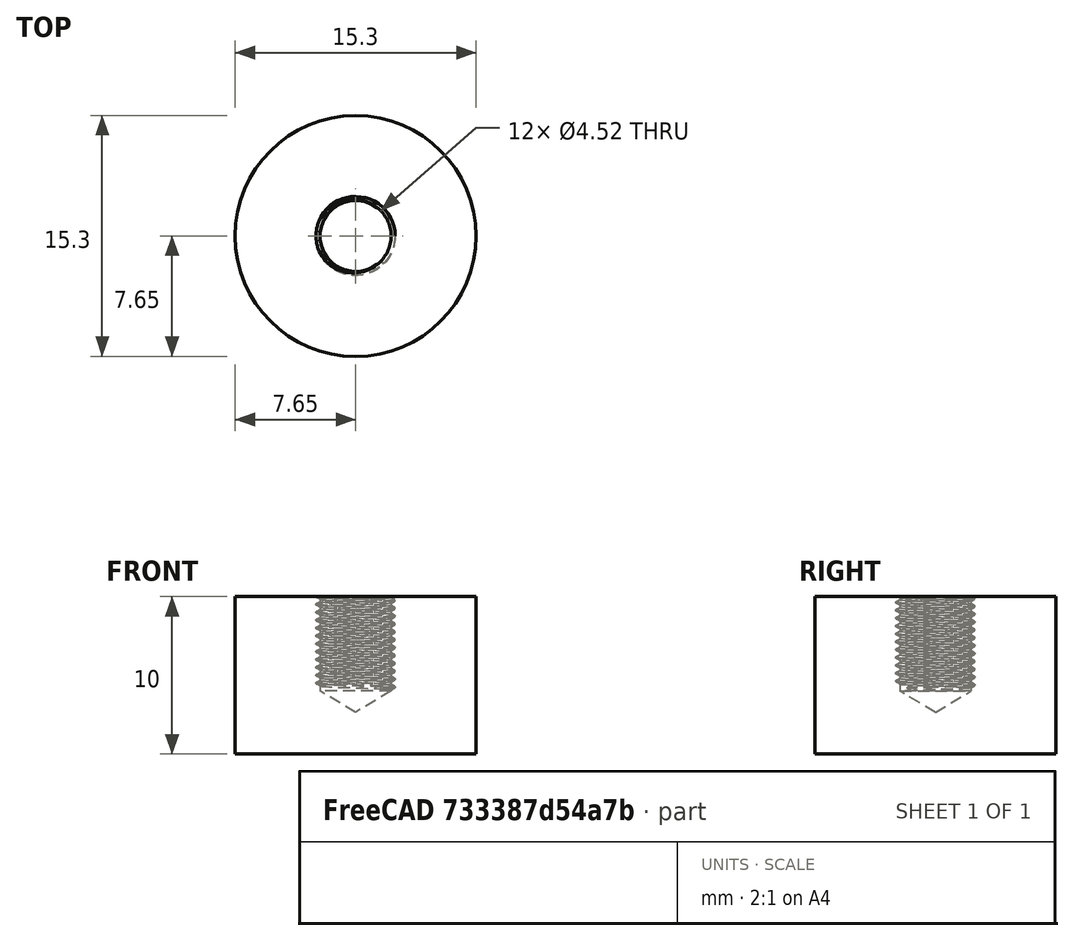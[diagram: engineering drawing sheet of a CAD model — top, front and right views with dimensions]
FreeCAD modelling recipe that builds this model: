
FCSTD DOCUMENT  (FreeCAD 0.20R29603 (Git))
Label: Plug
License: All rights reserved
LicenseURL: http://en.wikipedia.org/wiki/All_rights_reserved
objects: Sketcher::SketchObject×1, PartDesign::Pad×1, PartDesign::Hole×1, PartDesign::Body×1
note: 6 computed .brp shape members not serialized (recipe doc carries the construction recipe); baked Part::Feature solids carry a one-line shape summary decoded from their .brp

FEATURE [Sketcher::SketchObject] Sketch
  FullyConstrained = true
  MapMode = 5
  Support = -> [XY_Plane]
  sketch-geometry (1):
    g0: Circle CenterX=0 CenterY=0 CenterZ=0 NormalX=0 NormalY=0 NormalZ=1 AngleXU=0 Radius=7.65
  constraints (2):
    c: Coincident(g0,g-1)
    c: Diameter(g0) = 15.3
FEATURE [PartDesign::Pad] Pad
  Direction = (0,0,1)
  Length = 10
  Length2 = 10
  Profile = -> Sketch
  ReferenceAxis = -> Sketch [N_Axis]
  Type = 0
FEATURE [PartDesign::Hole] Hole
  BaseFeature = -> Pad
  CustomThreadClearance = 0
  Depth = 6
  DepthType = 0
  Diameter = 4.52
  DrillForDepth = false
  DrillPoint = 1
  DrillPointAngle = 118
  HoleCutCountersinkAngle = 90
  HoleCutCustomValues = false
  HoleCutDepth = 0
  HoleCutDiameter = 6.1
  HoleCutType = 0
  ModelThread = true
  Profile = -> Pad [Face3]
  Tapered = false
  TaperedAngle = 90
  ThreadClass = 0
  ThreadDepth = 6
  ThreadDepthType = 0
  ThreadDirection = 0
  ThreadFit = 0
  ThreadSize = 13
  ThreadType = 2
  Threaded = true
  UseCustomThreadClearance = false
FEATURE [PartDesign::Body] Body
  Group = -> [Sketch,Pad,Hole]
  Origin = -> Origin
  Tip = -> Hole
